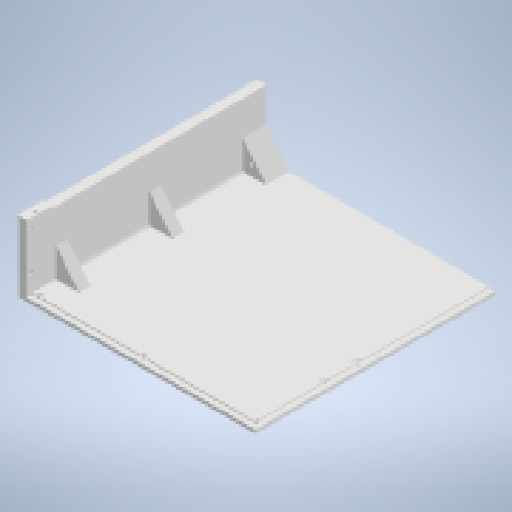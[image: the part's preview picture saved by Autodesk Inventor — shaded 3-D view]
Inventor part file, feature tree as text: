
AUTODESK INVENTOR PART (.ipt)
format: ipt  version: 2025.2 (Build 292293000, 293)  size: 646,656 bytes
history: native  units: mm
features: extrude x12, sketch x12, fillet x3, other x1
ambient origin geometry x8: Origin, YZ Plane, XZ Plane, XY Plane, X Axis, Y Axis, Z Axis, Center Point
bodies: Body1 (feature_tree)
feature tree (28):
  other  "ソリッド1"
  extrude  "押し出し1"  Depth=204.0mm
  extrude  "押し出し2"  Depth=205.0mm
  extrude  "押し出し3"  Depth=5.0mm TaperAngle=0.0deg
  extrude  "押し出し4"  Depth=8.0mm
  extrude  "押し出し5"  Depth=56.0mm TaperAngle=0.0deg
  extrude  "押し出し6"  Depth=3.0mm
  extrude  "押し出し7"  Depth=10.0mm
  fillet  "フィレット1"  Radius=5.5mm
  extrude  "押し出し8"  Depth=12.0mm TaperAngle=0.0deg
  fillet  "フィレット2"  Radius=3.0mm
  extrude  "押し出し9"  Depth=3.0mm
  extrude  "押し出し10"  Depth=20.0mm
  fillet  "フィレット3"  Radius=33.0mm
  extrude  "押し出し11"  TaperAngle=0.0deg  [1 undecoded]
  extrude  "押し出し12"  Depth=4.0mm
  sketch  "スケッチ1"
  sketch  "スケッチ2"
  sketch  "スケッチ3"
  sketch  "スケッチ4"
  sketch  "スケッチ5"
  sketch  "スケッチ7"
  sketch  "スケッチ8"
  sketch  "スケッチ9"
  sketch  "スケッチ10"
  sketch  "スケッチ11"
  sketch  "スケッチ12"
  sketch  "スケッチ13"
note: 1 required parameter value undecoded (feature->parameter linkage not recoverable at this tier; creation-order binding heuristic only, values carry confidence <= 0.55)
